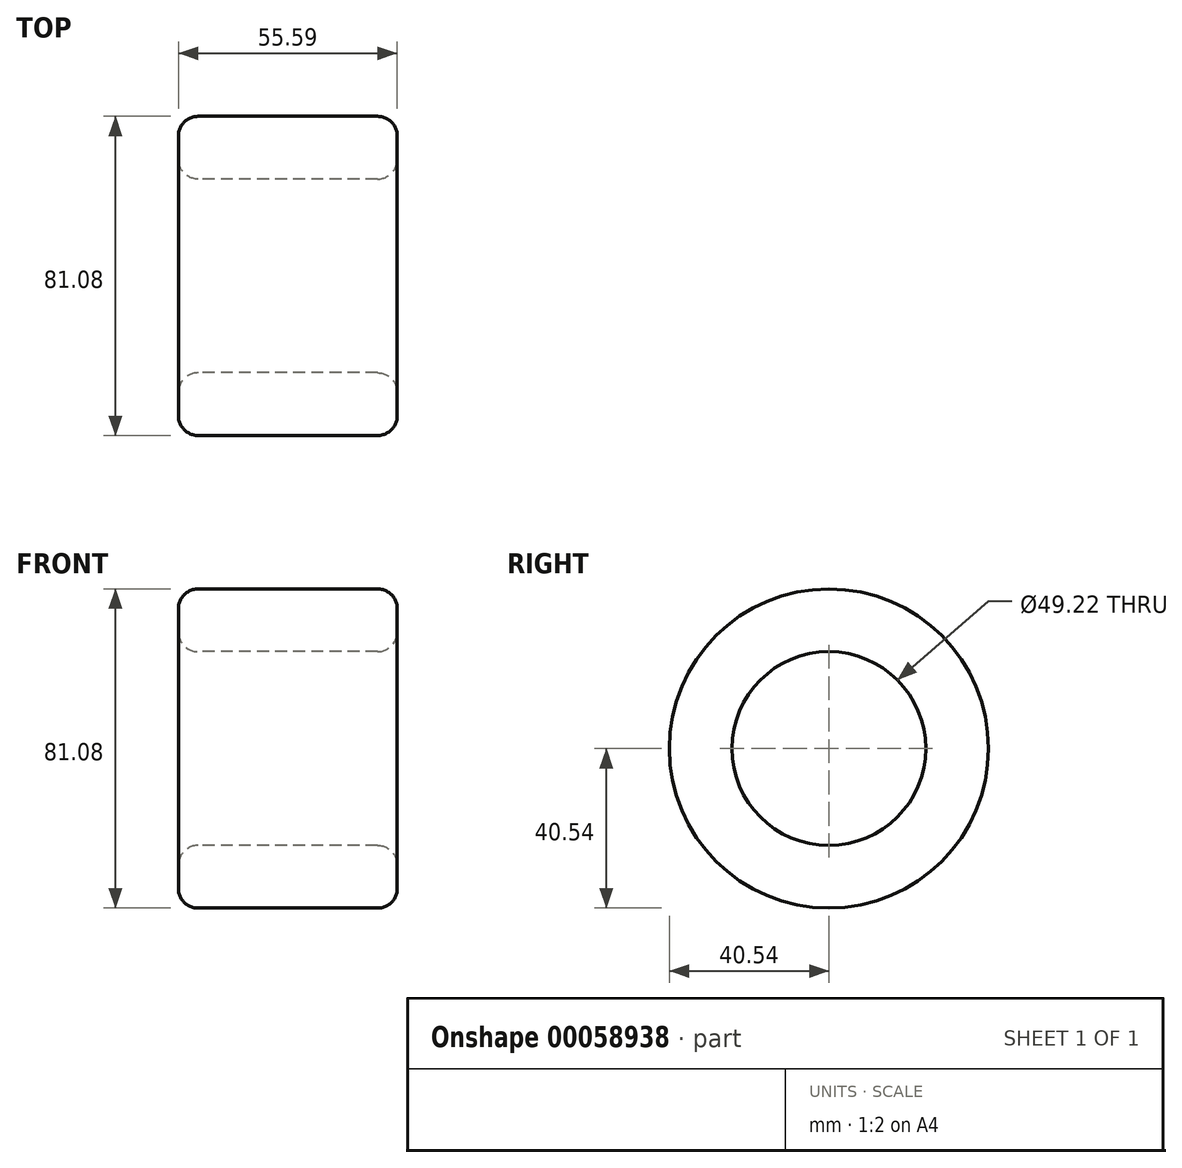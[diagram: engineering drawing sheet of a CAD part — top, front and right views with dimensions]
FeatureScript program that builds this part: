
annotation { "Feature Type Name" : "Feature", "Feature Type Description" : "" }
export const myFeature = defineFeature(function(context is Context, id is Id, definition is map)
    precondition{}
    {
        {
            var Q0;
            Q0=qCreatedBy(makeId("Front.planeOp"),FACE);
            var sketch = newSketch(context, id + "F0", { "sketchPlane" : qUnion([Q0])});
            skLineSegment(sketch, "E0.bottom", {"start": v(-21.6, 24.6) * mm, "end": v(34, 24.6) * mm});
            skLineSegment(sketch, "E0.top", {"start": v(-21.6, 40.54) * mm, "end": v(34, 40.54) * mm});
            skLineSegment(sketch, "E0.left", {"start": v(-21.6, 24.6) * mm, "end": v(-21.6, 40.54) * mm});
            skLineSegment(sketch, "E0.right", {"start": v(34, 24.6) * mm, "end": v(34, 40.54) * mm});
            skLineSegment(sketch, "E1", {"start": v(-30.45, 0) * mm, "end": v(42.85, 0) * mm});
            skSolve(sketch);
        }
        {
            var Q0;
            Q0 = qSketchRegion(id + "F0", true);
            var Q1;
            Q1=sQuery(id+"F0.wireOp",EDGE,"E1");
            revolve(context, id + "F1", {"entities" : qUnion([Q0]), "axis" : qUnion([Q1]), "revolveType" : RevolveType.FULL});
        }
        {
            var Q0;
            Q0=makeQuery(id+"F1.opRevolve","SWEPT_FACE",FACE,{"disambiguationData":[OSD([sQuery(id+"F0.wireOp",EDGE,"E0.left")])]});
            var Q1;
            Q1=makeQuery(id+"F1.opRevolve","SWEPT_FACE",FACE,{"disambiguationData":[OSD([sQuery(id+"F0.wireOp",EDGE,"E0.right")])]});
            fillet(context, id + "F2", {"entities" : qUnion([Q0, Q1]), "radius" : 5 * mm, "tangentPropagation" : true, "allowEdgeOverflow" : false});
        }
    });
